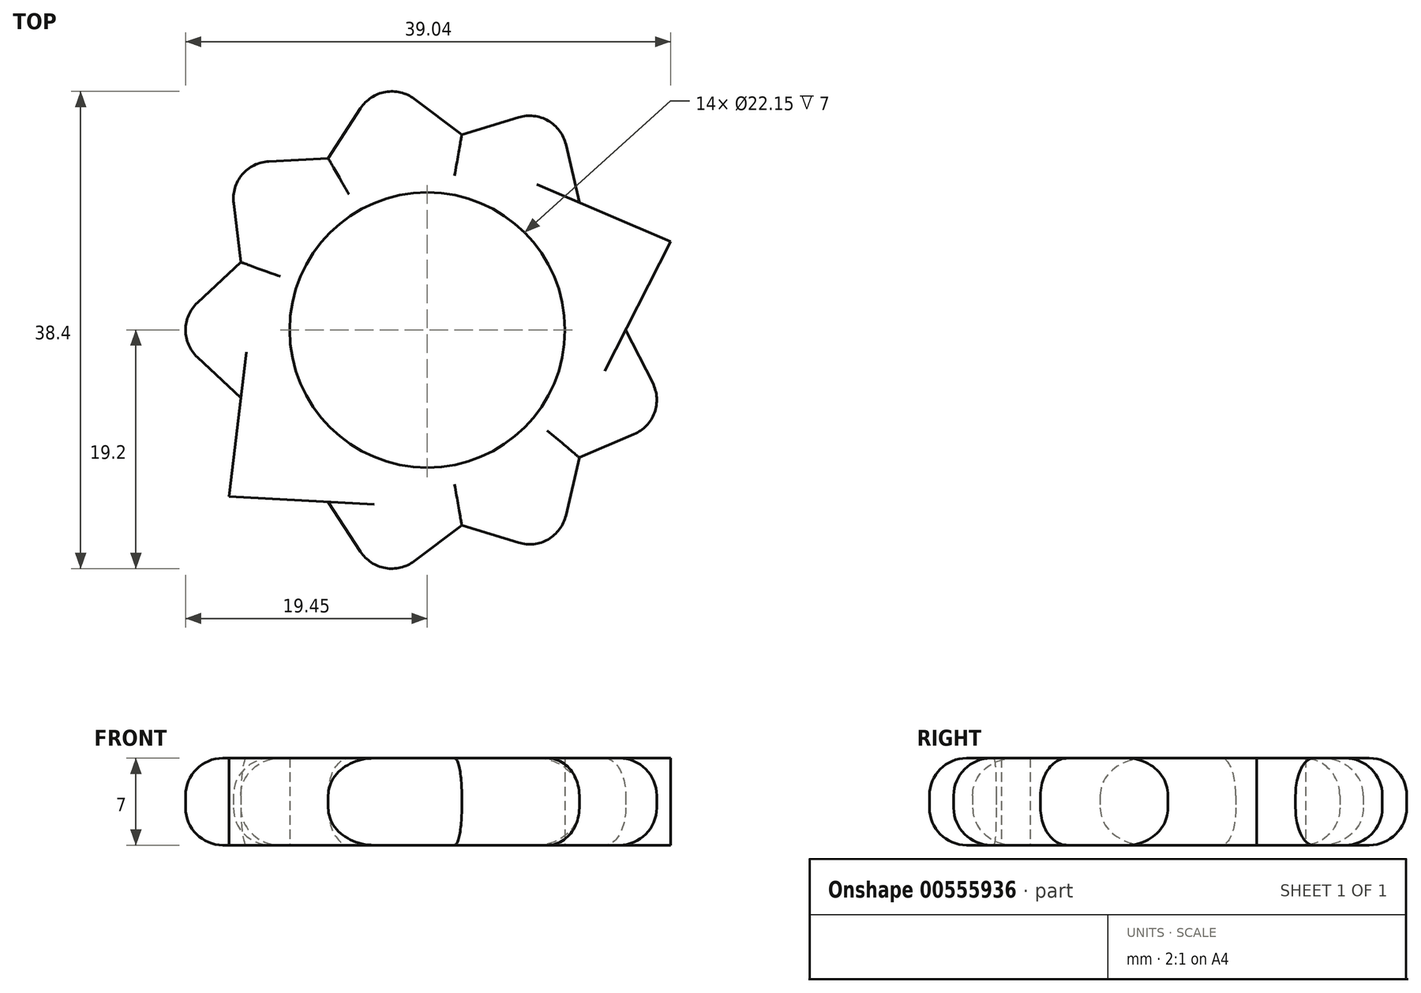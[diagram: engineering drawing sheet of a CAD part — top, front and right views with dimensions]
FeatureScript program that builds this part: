
annotation { "Feature Type Name" : "Feature", "Feature Type Description" : "" }
export const myFeature = defineFeature(function(context is Context, id is Id, definition is map)
    precondition{}
    {
        {
            var Q0;
            Q0=qCreatedBy(makeId("Top.planeOp"),FACE);
            var sketch = newSketch(context, id + "F0", { "sketchPlane" : qUnion([Q0])});
            skCircle(sketch, "E0", {"center": v(0, 0) * mm, "radius": 11.07 * mm});
            skCircle(sketch, "E1", {"center": v(0, 0) * mm, "radius": 15 * mm});
            skCircle(sketch, "E2.cCircle", {"center": v(0, 0) * mm, "radius": 15 * mm, "construction": true});
            skLineSegment(sketch, "E2.0", {"start": v(-15, -5.46) * mm, "end": v(-15, 5.46) * mm});
            skLineSegment(sketch, "E2.1", {"start": v(-15, 5.46) * mm, "end": v(-7.98, 13.82) * mm});
            skLineSegment(sketch, "E2.2", {"start": v(-7.98, 13.82) * mm, "end": v(2.77, 15.72) * mm});
            skLineSegment(sketch, "E2.3", {"start": v(2.77, 15.72) * mm, "end": v(12.23, 10.26) * mm});
            skLineSegment(sketch, "E2.4", {"start": v(12.23, 10.26) * mm, "end": v(15.96, 0) * mm});
            skLineSegment(sketch, "E2.5", {"start": v(15.96, 0) * mm, "end": v(12.23, -10.26) * mm});
            skLineSegment(sketch, "E2.6", {"start": v(12.23, -10.26) * mm, "end": v(2.77, -15.72) * mm});
            skLineSegment(sketch, "E2.7", {"start": v(2.77, -15.72) * mm, "end": v(-7.98, -13.82) * mm});
            skLineSegment(sketch, "E2.8", {"start": v(-7.98, -13.82) * mm, "end": v(-15, -5.46) * mm});
            skPoint(sketch, "E2.0.midPoint", {"position": v(-15, 0) * mm});
            skLineSegment(sketch, "E3", {"start": v(-15, 5.46) * mm, "end": v(-15.58, 10.21) * mm});
            skLineSegment(sketch, "E4.MirrorCS", {"start": v(-7.98, 13.82) * mm, "end": v(-12.76, 13.57) * mm});
            skLineSegment(sketch, "E5.MirrorCS", {"start": v(12.23, 10.26) * mm, "end": v(19.59, 7.13) * mm});
            skLineSegment(sketch, "E6.MirrorCS", {"start": v(15.96, 0) * mm, "end": v(19.59, 7.13) * mm});
            skLineSegment(sketch, "E7.MirrorCS", {"start": v(15.96, 0) * mm, "end": v(18.13, -4.27) * mm});
            skLineSegment(sketch, "E8.MirrorCS", {"start": v(12.23, -10.26) * mm, "end": v(16.63, -8.39) * mm});
            skLineSegment(sketch, "E9.MirrorCS", {"start": v(-15, 5.46) * mm, "end": v(-18.5, 2.2) * mm});
            skLineSegment(sketch, "E10.MirrorCS", {"start": v(-15, -5.46) * mm, "end": v(-18.5, -2.2) * mm});
            skLineSegment(sketch, "E11.MirrorCS", {"start": v(-7.98, -13.82) * mm, "end": v(-15.97, -13.4) * mm});
            skLineSegment(sketch, "E12.MirrorCS", {"start": v(-15, -5.46) * mm, "end": v(-15.97, -13.4) * mm});
            skLineSegment(sketch, "E13.MirrorCS", {"start": v(2.77, 15.72) * mm, "end": v(7.35, 17.11) * mm});
            skLineSegment(sketch, "E14.MirrorCS", {"start": v(12.23, 10.26) * mm, "end": v(11.15, 14.92) * mm});
            skLineSegment(sketch, "E15.MirrorCS", {"start": v(-7.98, 13.82) * mm, "end": v(-3.62, 20.53) * mm});
            skLineSegment(sketch, "E16.MirrorCS", {"start": v(2.77, 15.72) * mm, "end": v(-3.62, 20.53) * mm});
            skLineSegment(sketch, "E17.MirrorCS", {"start": v(-7.98, -13.82) * mm, "end": v(-3.62, -20.53) * mm});
            skLineSegment(sketch, "E18.MirrorCS", {"start": v(2.77, -15.72) * mm, "end": v(-3.62, -20.53) * mm});
            skLineSegment(sketch, "E19.MirrorCS", {"start": v(2.77, -15.72) * mm, "end": v(7.35, -17.11) * mm});
            skLineSegment(sketch, "E20.MirrorCS", {"start": v(12.23, -10.26) * mm, "end": v(11.15, -14.92) * mm});
            skPoint(sketch, "E21.visualSharp", {"position": v(-15.97, 13.4) * mm});
            skArc(sketch, "E21.filletArc", {"start": v(-12.76, 13.57) * mm, "mid": v(-14.9, 12.5) * mm, "end": v(-15.58, 10.21) * mm});
            skPoint(sketch, "E22.visualSharp", {"position": v(10.42, -18.05) * mm});
            skArc(sketch, "E22.filletArc", {"start": v(7.35, -17.11) * mm, "mid": v(9.72, -16.84) * mm, "end": v(11.15, -14.92) * mm});
            skPoint(sketch, "E23.visualSharp", {"position": v(19.59, -7.13) * mm});
            skArc(sketch, "E23.filletArc", {"start": v(16.63, -8.39) * mm, "mid": v(18.28, -6.65) * mm, "end": v(18.13, -4.27) * mm});
            skPoint(sketch, "E24.visualSharp", {"position": v(10.42, 18.05) * mm});
            skArc(sketch, "E24.filletArc", {"start": v(11.15, 14.92) * mm, "mid": v(9.72, 16.84) * mm, "end": v(7.35, 17.11) * mm});
            skPoint(sketch, "E25.visualSharp", {"position": v(-20.84, 0) * mm});
            skArc(sketch, "E25.filletArc", {"start": v(-18.5, 2.2) * mm, "mid": v(-19.45, 0) * mm, "end": v(-18.5, -2.2) * mm});
            skSolve(sketch);
        }
        {
            var Q0;
            Q0=qSketchRegion(id+"F0",true);
            var Q1;
            Q1=makeQuery(id+"F0.imprint","IMPRINT",FACE,{"disambiguationData":[TD([[makeQuery(id+"F0.imprint","IMPRINT",EDGE,{"derivedFrom":sQuery(id+"F0.wireOp",EDGE,"E0")}),-1.0]])]});
            extrude(context, id + "F1", {"entities" : qUnion([Q0, Q1]), "depth" : 7 * mm, "offsetDistance" : 25 * mm});
        }
        {
            var Q0;
            Q0=makeQuery(id+"F1.opExtrude","CAP_EDGE",EDGE,{"disambiguationData":[OSD([sQuery(id+"F0.wireOp",EDGE,"E15.MirrorCS")])],"isStart":false});
            var Q1;
            Q1=makeQuery(id+"F1.opExtrude","CAP_EDGE",EDGE,{"disambiguationData":[OSD([sQuery(id+"F0.wireOp",EDGE,"E16.MirrorCS")])],"isStart":false});
            var Q2;
            Q2=makeQuery(id+"F1.opExtrude","CAP_EDGE",EDGE,{"disambiguationData":[OSD([sQuery(id+"F0.wireOp",EDGE,"E16.MirrorCS")])],"isStart":true});
            var Q3;
            Q3=makeQuery(id+"F1.opExtrude","CAP_EDGE",EDGE,{"disambiguationData":[OSD([sQuery(id+"F0.wireOp",EDGE,"E4.MirrorCS")])],"isStart":false});
            var Q4;
            Q4=makeQuery(id+"F1.opExtrude","CAP_EDGE",EDGE,{"disambiguationData":[OSD([sQuery(id+"F0.wireOp",EDGE,"E9.MirrorCS")])],"isStart":false});
            var Q5;
            Q5=makeQuery(id+"F1.opExtrude","CAP_EDGE",EDGE,{"disambiguationData":[OSD([sQuery(id+"F0.wireOp",EDGE,"E10.MirrorCS")])],"isStart":false});
            var Q6;
            Q6=makeQuery(id+"F1.opExtrude","CAP_EDGE",EDGE,{"disambiguationData":[OSD([sQuery(id+"F0.wireOp",EDGE,"E9.MirrorCS")])],"isStart":true});
            var Q7;
            Q7=makeQuery(id+"F1.opExtrude","CAP_EDGE",EDGE,{"disambiguationData":[OSD([sQuery(id+"F0.wireOp",EDGE,"E10.MirrorCS")])],"isStart":true});
            var Q8;
            Q8=makeQuery(id+"F1.opExtrude","CAP_EDGE",EDGE,{"disambiguationData":[OSD([sQuery(id+"F0.wireOp",EDGE,"E12.MirrorCS")])],"isStart":false});
            var Q9;
            Q9=makeQuery(id+"F1.opExtrude","CAP_EDGE",EDGE,{"disambiguationData":[OSD([sQuery(id+"F0.wireOp",EDGE,"E17.MirrorCS")])],"isStart":false});
            var Q10;
            Q10=makeQuery(id+"F1.opExtrude","CAP_EDGE",EDGE,{"disambiguationData":[OSD([sQuery(id+"F0.wireOp",EDGE,"E11.MirrorCS")])],"isStart":false});
            var Q11;
            Q11=makeQuery(id+"F1.opExtrude","CAP_EDGE",EDGE,{"disambiguationData":[OSD([sQuery(id+"F0.wireOp",EDGE,"E18.MirrorCS")])],"isStart":false});
            var Q12;
            Q12=makeQuery(id+"F1.opExtrude","CAP_EDGE",EDGE,{"disambiguationData":[OSD([sQuery(id+"F0.wireOp",EDGE,"E19.MirrorCS")])],"isStart":false});
            var Q13;
            Q13=makeQuery(id+"F1.opExtrude","CAP_EDGE",EDGE,{"disambiguationData":[OSD([sQuery(id+"F0.wireOp",EDGE,"E20.MirrorCS")])],"isStart":false});
            var Q14;
            Q14=makeQuery(id+"F1.opExtrude","CAP_EDGE",EDGE,{"disambiguationData":[OSD([sQuery(id+"F0.wireOp",EDGE,"E8.MirrorCS")])],"isStart":false});
            var Q15;
            Q15=makeQuery(id+"F1.opExtrude","CAP_EDGE",EDGE,{"disambiguationData":[OSD([sQuery(id+"F0.wireOp",EDGE,"E6.MirrorCS")])],"isStart":false});
            var Q16;
            Q16=makeQuery(id+"F1.opExtrude","CAP_EDGE",EDGE,{"disambiguationData":[OSD([sQuery(id+"F0.wireOp",EDGE,"E14.MirrorCS")])],"isStart":false});
            var Q17;
            Q17=makeQuery(id+"F1.opExtrude","CAP_EDGE",EDGE,{"disambiguationData":[OSD([sQuery(id+"F0.wireOp",EDGE,"E7.MirrorCS")])],"isStart":false});
            var Q18;
            Q18=makeQuery(id+"F1.opExtrude","CAP_EDGE",EDGE,{"disambiguationData":[OSD([sQuery(id+"F0.wireOp",EDGE,"E13.MirrorCS")])],"isStart":false});
            var Q19;
            Q19=makeQuery(id+"F1.opExtrude","CAP_EDGE",EDGE,{"disambiguationData":[OSD([sQuery(id+"F0.wireOp",EDGE,"E5.MirrorCS")])],"isStart":false});
            var Q20;
            Q20=makeQuery(id+"F1.opExtrude","CAP_EDGE",EDGE,{"disambiguationData":[OSD([sQuery(id+"F0.wireOp",EDGE,"E3")])],"isStart":false});
            var Q21;
            Q21=makeQuery(id+"F1.opExtrude","CAP_EDGE",EDGE,{"disambiguationData":[OSD([sQuery(id+"F0.wireOp",EDGE,"E6.MirrorCS")])],"isStart":true});
            var Q22;
            Q22=makeQuery(id+"F1.opExtrude","SWEPT_EDGE",EDGE,{"disambiguationData":[OSD([sQuery(id+"F0.wireOp",EDGE,"E6.MirrorCS"),sQuery(id+"F0.wireOp",EDGE,"E5.MirrorCS")])]});
            var Q23;
            Q23=makeQuery(id+"F1.opExtrude","CAP_EDGE",EDGE,{"disambiguationData":[OSD([sQuery(id+"F0.wireOp",EDGE,"E8.MirrorCS")])],"isStart":true});
            var Q24;
            Q24=makeQuery(id+"F1.opExtrude","CAP_EDGE",EDGE,{"disambiguationData":[OSD([sQuery(id+"F0.wireOp",EDGE,"E20.MirrorCS")])],"isStart":true});
            var Q25;
            Q25=makeQuery(id+"F1.opExtrude","CAP_EDGE",EDGE,{"disambiguationData":[OSD([sQuery(id+"F0.wireOp",EDGE,"E19.MirrorCS")])],"isStart":true});
            var Q26;
            Q26=makeQuery(id+"F1.opExtrude","CAP_EDGE",EDGE,{"disambiguationData":[OSD([sQuery(id+"F0.wireOp",EDGE,"E17.MirrorCS")])],"isStart":true});
            var Q27;
            Q27=makeQuery(id+"F1.opExtrude","CAP_EDGE",EDGE,{"disambiguationData":[OSD([sQuery(id+"F0.wireOp",EDGE,"E12.MirrorCS")])],"isStart":true});
            var Q28;
            Q28=makeQuery(id+"F1.opExtrude","CAP_EDGE",EDGE,{"disambiguationData":[OSD([sQuery(id+"F0.wireOp",EDGE,"E3")])],"isStart":true});
            var Q29;
            Q29=makeQuery(id+"F1.opExtrude","CAP_EDGE",EDGE,{"disambiguationData":[OSD([sQuery(id+"F0.wireOp",EDGE,"E4.MirrorCS")])],"isStart":true});
            var Q30;
            Q30=makeQuery(id+"F1.opExtrude","CAP_EDGE",EDGE,{"disambiguationData":[OSD([sQuery(id+"F0.wireOp",EDGE,"E14.MirrorCS")])],"isStart":true});
            var Q31;
            Q31=makeQuery(id+"F1.opExtrude","CAP_EDGE",EDGE,{"disambiguationData":[OSD([sQuery(id+"F0.wireOp",EDGE,"E15.MirrorCS")])],"isStart":true});
            var Q32;
            Q32=makeQuery(id+"F1.opExtrude","CAP_EDGE",EDGE,{"disambiguationData":[OSD([sQuery(id+"F0.wireOp",EDGE,"E11.MirrorCS")])],"isStart":true});
            var Q33;
            Q33=makeQuery(id+"F1.opExtrude","CAP_EDGE",EDGE,{"disambiguationData":[OSD([sQuery(id+"F0.wireOp",EDGE,"E18.MirrorCS")])],"isStart":true});
            var Q34;
            Q34=makeQuery(id+"F1.opExtrude","CAP_EDGE",EDGE,{"disambiguationData":[OSD([sQuery(id+"F0.wireOp",EDGE,"E7.MirrorCS")])],"isStart":true});
            fillet(context, id + "F2", {"entities" : qUnion([Q0, Q1, Q2, Q3, Q4, Q5, Q6, Q7, Q8, Q9, Q10, Q11, Q12, Q13, Q14, Q15, Q16, Q17, Q18, Q19, Q20, Q21, Q22, Q23, Q24, Q25, Q26, Q27, Q28, Q29, Q30, Q31, Q32, Q33, Q34]), "radius" : 3 * mm, "tangentPropagation" : true, "allowEdgeOverflow" : false});
        }
        {
            var Q0;
            Q0=makeQuery(id+"F1.opExtrude","CAP_EDGE",EDGE,{"disambiguationData":[OSD([sQuery(id+"F0.wireOp",EDGE,"E5.MirrorCS")])],"isStart":true});
            var Q1;
            Q1=makeQuery(id+"F2.opFillet","BLEND_EDGE",EDGE,{"blendedFrom":[makeQuery(id+"F1.opExtrude","CAP_EDGE",EDGE,{"disambiguationData":[OSD([sQuery(id+"F0.wireOp",EDGE,"E18.MirrorCS")])],"isStart":false}),makeQuery(id+"F1.opExtrude","CAP_EDGE",EDGE,{"disambiguationData":[OSD([sQuery(id+"F0.wireOp",EDGE,"E17.MirrorCS")])],"isStart":false})],"blendedInto":[]});
            var Q2;
            Q2=makeQuery(id+"F2.opFillet","BLEND_EDGE",EDGE,{"blendedFrom":[makeQuery(id+"F1.opExtrude","CAP_EDGE",EDGE,{"disambiguationData":[OSD([sQuery(id+"F0.wireOp",EDGE,"E11.MirrorCS")])],"isStart":true}),makeQuery(id+"F1.opExtrude","CAP_EDGE",EDGE,{"disambiguationData":[OSD([sQuery(id+"F0.wireOp",EDGE,"E12.MirrorCS")])],"isStart":true})],"blendedInto":[]});
            var Q3;
            Q3=makeQuery(id+"F2.opFillet","BLEND_EDGE",EDGE,{"blendedFrom":[makeQuery(id+"F1.opExtrude","CAP_EDGE",EDGE,{"disambiguationData":[OSD([sQuery(id+"F0.wireOp",EDGE,"E15.MirrorCS")])],"isStart":true}),makeQuery(id+"F1.opExtrude","CAP_EDGE",EDGE,{"disambiguationData":[OSD([sQuery(id+"F0.wireOp",EDGE,"E16.MirrorCS")])],"isStart":true})],"blendedInto":[]});
            fillet(context, id + "F3", {"entities" : qUnion([Q0, Q1, Q2, Q3]), "radius" : 3 * mm, "tangentPropagation" : true, "allowEdgeOverflow" : false});
        }
    });
